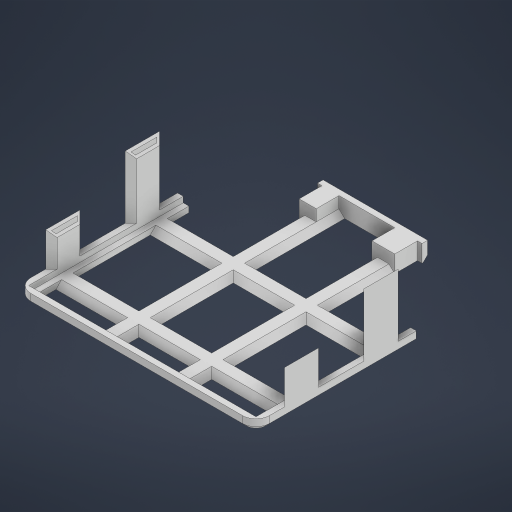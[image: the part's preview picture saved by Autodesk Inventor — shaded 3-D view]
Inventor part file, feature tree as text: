
AUTODESK INVENTOR PART (.ipt)
format: ipt  version: 2024 (Build 280153000, 153)  size: 538,624 bytes
history: native  units: mm
features: extrude x12, sketch x8, projected_geometry x7, other x1, fillet x1, chamfer x1
ambient origin geometry x8: Origin, YZ Plane, XZ Plane, XY Plane, X Axis, Y Axis, Z Axis, Center Point
bodies: Body1 (feature_tree)
feature tree (30):
  other  "Těleso1"
  sketch  "Náčrt1"
  extrude  "Vysunutí1"  Depth=100.0mm
  extrude  "Vysunutí2"  Depth=2.5mm
  sketch  "Náčrt2"
  extrude  "Vysunutí3"  Depth=2.5mm
  sketch  "Náčrt3"
  extrude  "Vysunutí4"  Depth=68.0mm
  extrude  "Vysunutí5"  Depth=27.0mm
  extrude  "Vysunutí6"  Depth=27.0mm
  extrude  "Vysunutí7"  Depth=2.5mm TaperAngle=0.0deg
  extrude  "Vysunutí8"  Depth=5.0mm TaperAngle=0.0deg
  fillet  "Zaoblení1"  [1 undecoded]
  chamfer  "Zkosení1"  Distance=2.0mm
  sketch  "Náčrt6"
  extrude  "Vysunutí9"  Depth=2.0mm
  extrude  "Vysunutí10"  Depth=5.0mm
  extrude  "Vysunutí11"  Depth=5.0mm
  extrude  "Vysunutí12"  Depth=0.75mm
  sketch  "Náčrt4"
  projected_geometry  "Promítnutá smyčka1"
  sketch  "Náčrt5"
  projected_geometry  "Promítnutá smyčka2"
  projected_geometry  "Promítnutá smyčka3"
  sketch  "Náčrt7"
  projected_geometry  "Promítnutá smyčka4"
  projected_geometry  "Promítnutá smyčka5"
  sketch  "Náčrt8"
  projected_geometry  "Promítnutá smyčka6"
  projected_geometry  "Promítnutá smyčka7"
note: 1 required parameter value undecoded (feature->parameter linkage not recoverable at this tier; creation-order binding heuristic only, values carry confidence <= 0.55)
